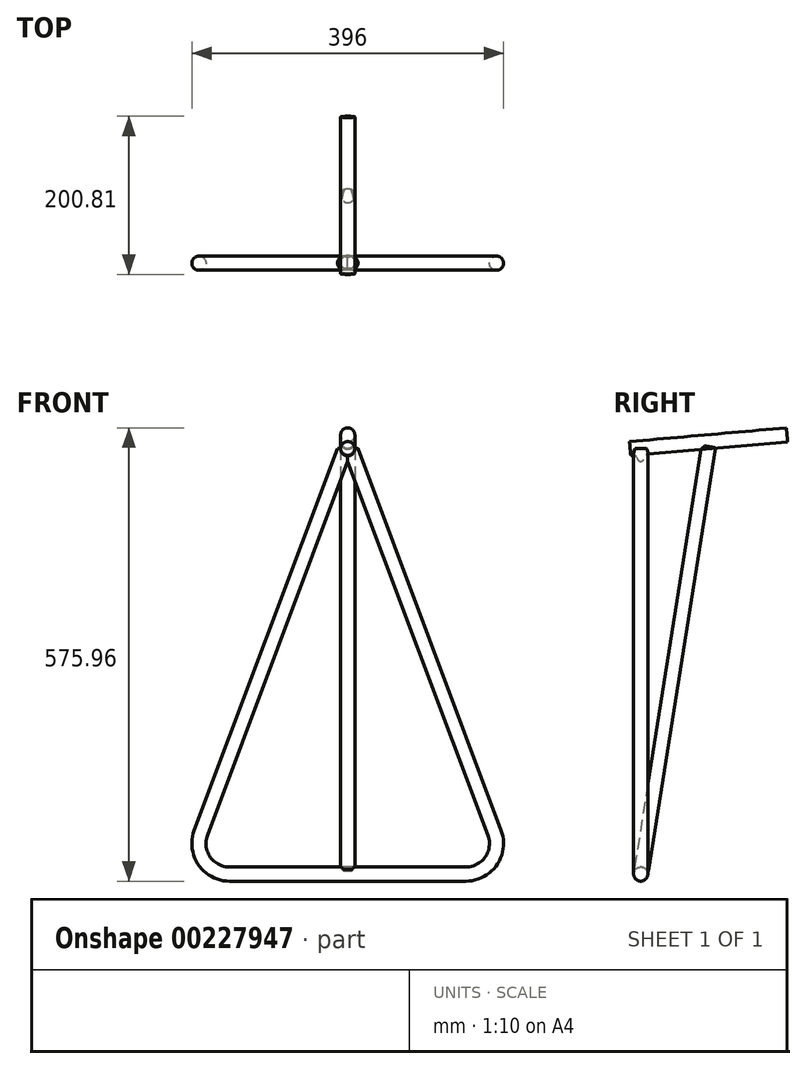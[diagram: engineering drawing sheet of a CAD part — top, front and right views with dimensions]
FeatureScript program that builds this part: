
annotation { "Feature Type Name" : "Feature", "Feature Type Description" : "" }
export const myFeature = defineFeature(function(context is Context, id is Id, definition is map)
    precondition{}
    {
        {
            var Q0;
            Q0=qCreatedBy(makeId("Front.planeOp"),FACE);
            var sketch = newSketch(context, id + "F0", { "sketchPlane" : qUnion([Q0])});
            skCircle(sketch, "E0", {"center": v(-150, 0) * mm, "radius": 30 * mm});
            skLineSegment(sketch, "E1", {"start": v(0, -284.41) * mm, "end": v(0, 543.87) * mm, "construction": true});
            skLineSegment(sketch, "E2", {"start": v(-150, -30) * mm, "end": v(150, -30) * mm});
            skCircle(sketch, "E3.MirrorC", {"center": v(150, 0) * mm, "radius": 30 * mm});
            skLineSegment(sketch, "E4", {"start": v(0, 485.37) * mm, "end": v(-178.09, 10.54) * mm});
            skLineSegment(sketch, "E5.MirrorCS", {"start": v(0, 485.37) * mm, "end": v(178.09, 10.54) * mm});
            skLineSegment(sketch, "E6.0", {"start": v(0, 511) * mm, "end": v(-186.52, 13.7) * mm});
            skArc(sketch, "E7", {"start": v(-186.52, 13.7) * mm, "mid": v(-182.06, -22.21) * mm, "end": v(-150, -39) * mm});
            skLineSegment(sketch, "E8", {"start": v(-150, -39) * mm, "end": v(150, -39) * mm});
            skLineSegment(sketch, "E9.0", {"start": v(0, 511) * mm, "end": v(186.52, 13.7) * mm});
            skArc(sketch, "E10", {"start": v(150, -39) * mm, "mid": v(182.06, -22.21) * mm, "end": v(186.52, 13.7) * mm});
            skCircle(sketch, "E11", {"center": v(0, 485.37) * mm, "radius": 8 * mm});
            skCircle(sketch, "E12", {"center": v(0, 462.6) * mm, "radius": 8 * mm});
            skLineSegment(sketch, "E13", {"start": v(-117.06, -47) * mm, "end": v(146.74, -47) * mm});
            skSolve(sketch);
        }
        {
            var Q0;
            {var subQ6=sQuery(id+"F0.wireOp",EDGE,"E2");Q0=makeQuery(id+"F0.imprint","IMPRINT",FACE,{"disambiguationData":[TD([[makeQuery(id+"F0.imprint","IMPRINT",EDGE,{"derivedFrom":subQ6}),1.0]])]});}
            var sketch = newSketch(context, id + "F1", { "sketchPlane" : qUnion([Q0])});
            skLineSegment(sketch, "E14.0", {"start": v(0, 511) * mm, "end": v(-186.52, 13.7) * mm});
            skArc(sketch, "E14.1", {"start": v(-186.52, 13.7) * mm, "mid": v(-182.06, -22.21) * mm, "end": v(-150, -39) * mm});
            skLineSegment(sketch, "E14.2", {"start": v(-150, -39) * mm, "end": v(150, -39) * mm});
            skLineSegment(sketch, "E14.3", {"start": v(0, 511) * mm, "end": v(186.52, 13.7) * mm});
            skArc(sketch, "E14.4", {"start": v(150, -39) * mm, "mid": v(182.06, -22.21) * mm, "end": v(186.52, 13.7) * mm});
            skSolve(sketch);
        }
        {
            var Q0;
            Q0=sQuery(id+"F1.wireOp",VERTEX,"E14.4.start");
            var Q1;
            Q1=sQuery(id+"F1.wireOp",EDGE,"E14.2");
            cPlane(context, id + "F2", {"entities" : qUnion([Q0, Q1]), "cplaneType" : CPlaneType.CURVE_POINT, "offset" : 25 * mm, "width" : 150 * mm, "height" : 150 * mm});
        }
        {
            var Q0;
            Q0=qCreatedBy(id+"F2.planeOp",FACE);
            var sketch = newSketch(context, id + "F3", { "sketchPlane" : qUnion([Q0])});
            skCircle(sketch, "E15", {"center": v(0, -39) * mm, "radius": 9 * mm});
            skSolve(sketch);
        }
        {
            var Q0;
            Q0=makeQuery(id+"F3.imprint","IMPRINT",FACE,{"disambiguationData":[TD([[makeQuery(id+"F3.imprint","IMPRINT",EDGE,{"derivedFrom":sQuery(id+"F3.wireOp",EDGE,"E15")}),1.0]])]});
            var Q1;
            Q1=sQuery(id+"F1.wireOp",EDGE,"E14.2");
            var Q2;
            Q2=sQuery(id+"F1.wireOp",EDGE,"E14.4");
            var Q3;
            Q3=sQuery(id+"F1.wireOp",EDGE,"E14.1");
            var Q4;
            Q4=sQuery(id+"F1.wireOp",EDGE,"E14.0");
            var Q5;
            Q5=sQuery(id+"F1.wireOp",EDGE,"E14.3");
            sweep(context, id + "F4", {"profiles" : qUnion([Q0]), "path" : qUnion([Q1, Q2, Q3, Q4, Q5])});
        }
        {
            var Q0;
            Q0=qCreatedBy(makeId("Right.planeOp"),FACE);
            var sketch = newSketch(context, id + "F5", { "sketchPlane" : qUnion([Q0])});
            skLineSegment(sketch, "E16", {"start": v(0, 465.67) * mm, "end": v(144.94, 478.35) * mm});
            skSolve(sketch);
        }
        {
            var Q0;
            Q0=sQuery(id+"F0.wireOp",VERTEX,"E12.center");
            var Q1;
            Q1=sQuery(id+"F5.wireOp",EDGE,"E16");
            cPlane(context, id + "F6", {"entities" : qUnion([Q0, Q1]), "cplaneType" : CPlaneType.CURVE_POINT, "offset" : 25 * mm, "width" : 150 * mm, "height" : 150 * mm});
        }
        {
            var Q0;
            Q0=qCreatedBy(makeId("Front.planeOp"),FACE);
            var sketch = newSketch(context, id + "F7", { "sketchPlane" : qUnion([Q0])});
            skLineSegment(sketch, "E17.bottom", {"start": v(-89.17, 572.15) * mm, "end": v(122.26, 572.15) * mm});
            skLineSegment(sketch, "E17.top", {"start": v(-89.17, 502) * mm, "end": v(122.26, 502) * mm});
            skLineSegment(sketch, "E17.left", {"start": v(-89.17, 572.15) * mm, "end": v(-89.17, 502) * mm});
            skLineSegment(sketch, "E17.right", {"start": v(122.26, 572.15) * mm, "end": v(122.26, 502) * mm});
            skSolve(sketch);
        }
        {
            var Q0;
            Q0=makeQuery(id+"F7.imprint","IMPRINT",FACE,{"disambiguationData":[TD([[makeQuery(id+"F7.imprint","IMPRINT",EDGE,{"derivedFrom":sQuery(id+"F7.wireOp",EDGE,"E17.bottom")}),-1.0]])]});
            extrude(context, id + "F8", {"entities" : qUnion([Q0]), "operationType" : NewBodyOperationType.REMOVE, "oppositeDirection" : true, "depth" : 25 * mm, "symmetric" : true});
        }
        {
            var Q0;
            Q0=qCreatedBy(id+"F6.planeOp",FACE);
            var sketch = newSketch(context, id + "F9", { "sketchPlane" : qUnion([Q0])});
            skCircle(sketch, "E18", {"center": v(0, 500.82) * mm, "radius": 9 * mm});
            skSolve(sketch);
        }
        {
            var Q0;
            Q0=makeQuery(id+"F9.imprint","IMPRINT",FACE,{"disambiguationData":[TD([[makeQuery(id+"F9.imprint","IMPRINT",EDGE,{"derivedFrom":sQuery(id+"F9.wireOp",EDGE,"E18")}),1.0]])]});
            extrude(context, id + "F10", {"entities" : qUnion([Q0]), "operationType" : NewBodyOperationType.ADD, "depth" : 190 * mm, "hasSecondDirection" : true, "secondDirectionOppositeDirection" : true, "secondDirectionDepth" : 10 * mm});
        }
        {
            var Q0;
            Q0=qCreatedBy(makeId("Right.planeOp"),FACE);
            var sketch = newSketch(context, id + "F11", { "sketchPlane" : qUnion([Q0])});
            skLineSegment(sketch, "E19", {"start": v(-3.49, 502.43) * mm, "end": v(140.9, 515.06) * mm});
            skSolve(sketch);
        }
        {
            var Q0;
            Q0=qCreatedBy(makeId("Right.planeOp"),FACE);
            var sketch = newSketch(context, id + "F12", { "sketchPlane" : qUnion([Q0])});
            skLineSegment(sketch, "E20", {"start": v(0, -39) * mm, "end": v(87, 510.35) * mm});
            skSolve(sketch);
        }
        {
            var Q0;
            Q0=sQuery(id+"F0.wireOp",EDGE,"E8");
            cPoint(context, id + "F13", {"entities" : qUnion([Q0]), "parameter" : 0.5});
        }
        {
            var Q0;
            Q0=sQuery(id+"F12.wireOp",EDGE,"E20");
            var Q1;
            Q1 = qCreatedBy(id + "F13" ,VERTEX);
            cPlane(context, id + "F14", {"entities" : qUnion([Q0, Q1]), "cplaneType" : CPlaneType.CURVE_POINT, "offset" : 25 * mm, "width" : 150 * mm, "height" : 150 * mm});
        }
        {
            var Q0;
            Q0=qCreatedBy(id+"F14.planeOp",FACE);
            var sketch = newSketch(context, id + "F15", { "sketchPlane" : qUnion([Q0])});
            skCircle(sketch, "E21", {"center": v(0, 6.1) * mm, "radius": 9 * mm});
            skSolve(sketch);
        }
        {
            var Q0;
            Q0 = qSketchRegion(id + "F15", true);
            extrude(context, id + "F16", {"entities" : qUnion([Q0]), "depth" : 550 * mm, "hasSecondDirection" : true, "secondDirectionOppositeDirection" : false, "secondDirectionDepth" : 5 * mm});
        }
        {
            var Q0;
            Q0=makeQuery(id+"F4.opSweep","SWEPT_BODY",BODY,{"disambiguationData":[OSD([sQuery(id+"F1.wireOp",EDGE,"E14.1"),sQuery(id+"F3.wireOp",EDGE,"E15")])]});
            var Q1;
            Q1=makeQuery(id+"F16.opExtrude","SWEPT_BODY",BODY,{"disambiguationData":[OSD([sQuery(id+"F15.wireOp",EDGE,"E21")])]});
            booleanBodies(context, id + "F17", {"operationType" : BooleanOperationType.SUBTRACTION, "tools" : qUnion([Q0]), "targets" : qUnion([Q1]), "keepTools" : true});
        }
    });
